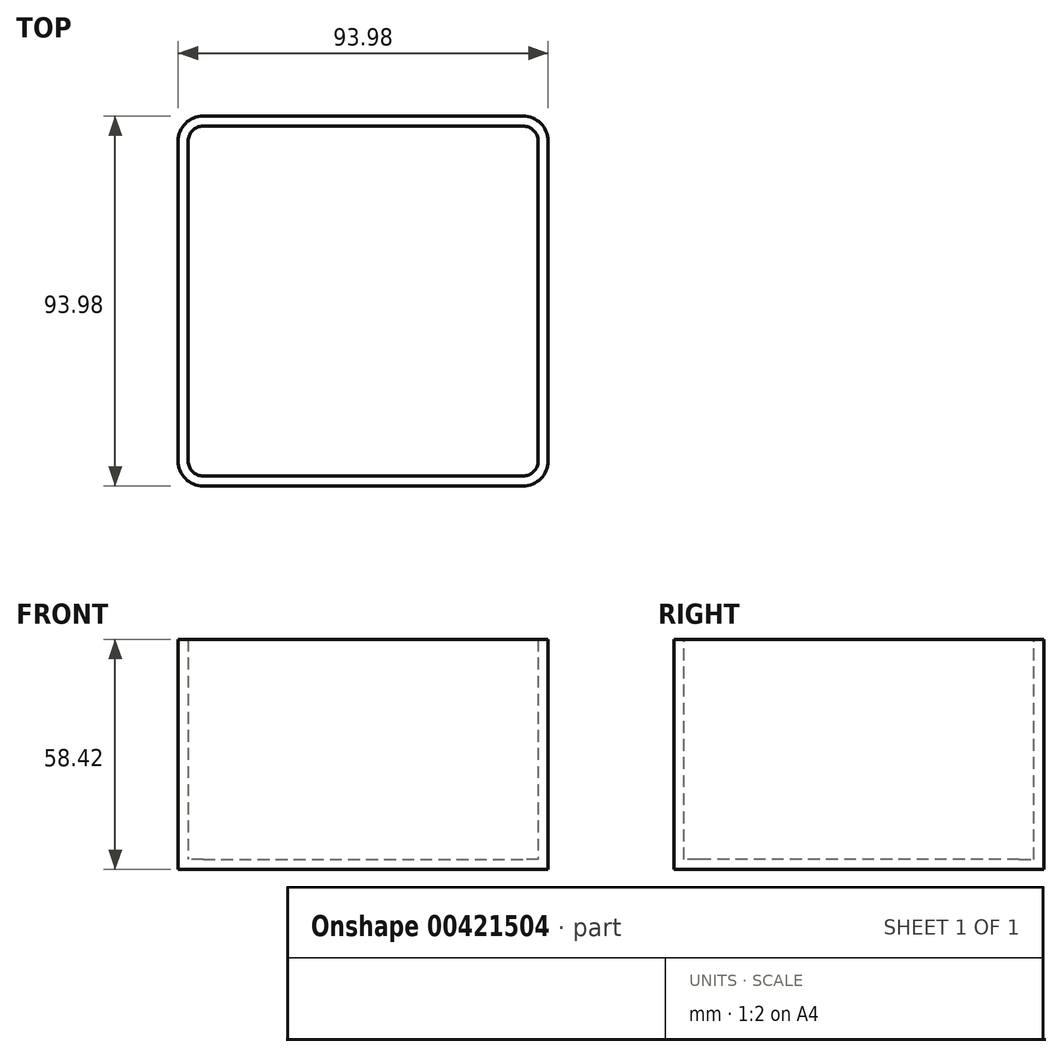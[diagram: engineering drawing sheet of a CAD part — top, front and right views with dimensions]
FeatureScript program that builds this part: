
annotation { "Feature Type Name" : "Feature", "Feature Type Description" : "" }
export const myFeature = defineFeature(function(context is Context, id is Id, definition is map)
    precondition{}
    {
        {
            var Q0;
            Q0=qCreatedBy(makeId("Top.planeOp"),FACE);
            var sketch = newSketch(context, id + "F0", { "sketchPlane" : qUnion([Q0])});
            skLineSegment(sketch, "E0.bottom", {"start": v(-16.5, 53.9) * mm, "end": v(64.77, 53.9) * mm});
            skLineSegment(sketch, "E0.top", {"start": v(-16.5, -40.08) * mm, "end": v(64.77, -40.08) * mm});
            skLineSegment(sketch, "E0.left", {"start": v(-22.86, 47.55) * mm, "end": v(-22.86, -33.73) * mm});
            skLineSegment(sketch, "E0.right", {"start": v(71.12, 47.55) * mm, "end": v(71.12, -33.73) * mm});
            skPoint(sketch, "E1.visualSharp", {"position": v(-22.86, 53.9) * mm});
            skArc(sketch, "E1.filletArc", {"start": v(-16.5, 53.9) * mm, "mid": v(-21, 52.04) * mm, "end": v(-22.86, 47.55) * mm});
            skPoint(sketch, "E2.visualSharp", {"position": v(71.12, 53.9) * mm});
            skArc(sketch, "E2.filletArc", {"start": v(71.12, 47.55) * mm, "mid": v(69.26, 52.04) * mm, "end": v(64.77, 53.9) * mm});
            skPoint(sketch, "E3.visualSharp", {"position": v(71.12, -40.08) * mm});
            skArc(sketch, "E3.filletArc", {"start": v(64.77, -40.08) * mm, "mid": v(69.26, -38.22) * mm, "end": v(71.12, -33.73) * mm});
            skPoint(sketch, "E4.visualSharp", {"position": v(-22.86, -40.08) * mm});
            skArc(sketch, "E4.filletArc", {"start": v(-22.86, -33.73) * mm, "mid": v(-21, -38.22) * mm, "end": v(-16.5, -40.08) * mm});
            skSolve(sketch);
        }
        {
            var Q0;
            Q0=makeQuery(id+"F0.imprint","IMPRINT",FACE,{"disambiguationData":[TD([[makeQuery(id+"F0.imprint","IMPRINT",EDGE,{"derivedFrom":sQuery(id+"F0.wireOp",EDGE,"E0.bottom")}),-1.0]])]});
            extrude(context, id + "F1", {"entities" : qUnion([Q0]), "depth" : 58.42 * mm});
        }
        {
            var Q0;
            Q0=makeQuery(id+"F1.opExtrude","CAP_FACE",FACE,{"disambiguationData":[OSD([sQuery(id+"F0.wireOp",EDGE,"E0.bottom"),sQuery(id+"F0.wireOp",EDGE,"E0.top"),sQuery(id+"F0.wireOp",EDGE,"E0.left"),sQuery(id+"F0.wireOp",EDGE,"E0.right"),sQuery(id+"F0.wireOp",EDGE,"E1.filletArc"),sQuery(id+"F0.wireOp",EDGE,"E2.filletArc"),sQuery(id+"F0.wireOp",EDGE,"E3.filletArc"),sQuery(id+"F0.wireOp",EDGE,"E4.filletArc")])],"isStart":false});
            shell(context, id + "F2", {"entities" : qUnion([Q0]), "thickness" : 2.54 * mm});
        }
    });
